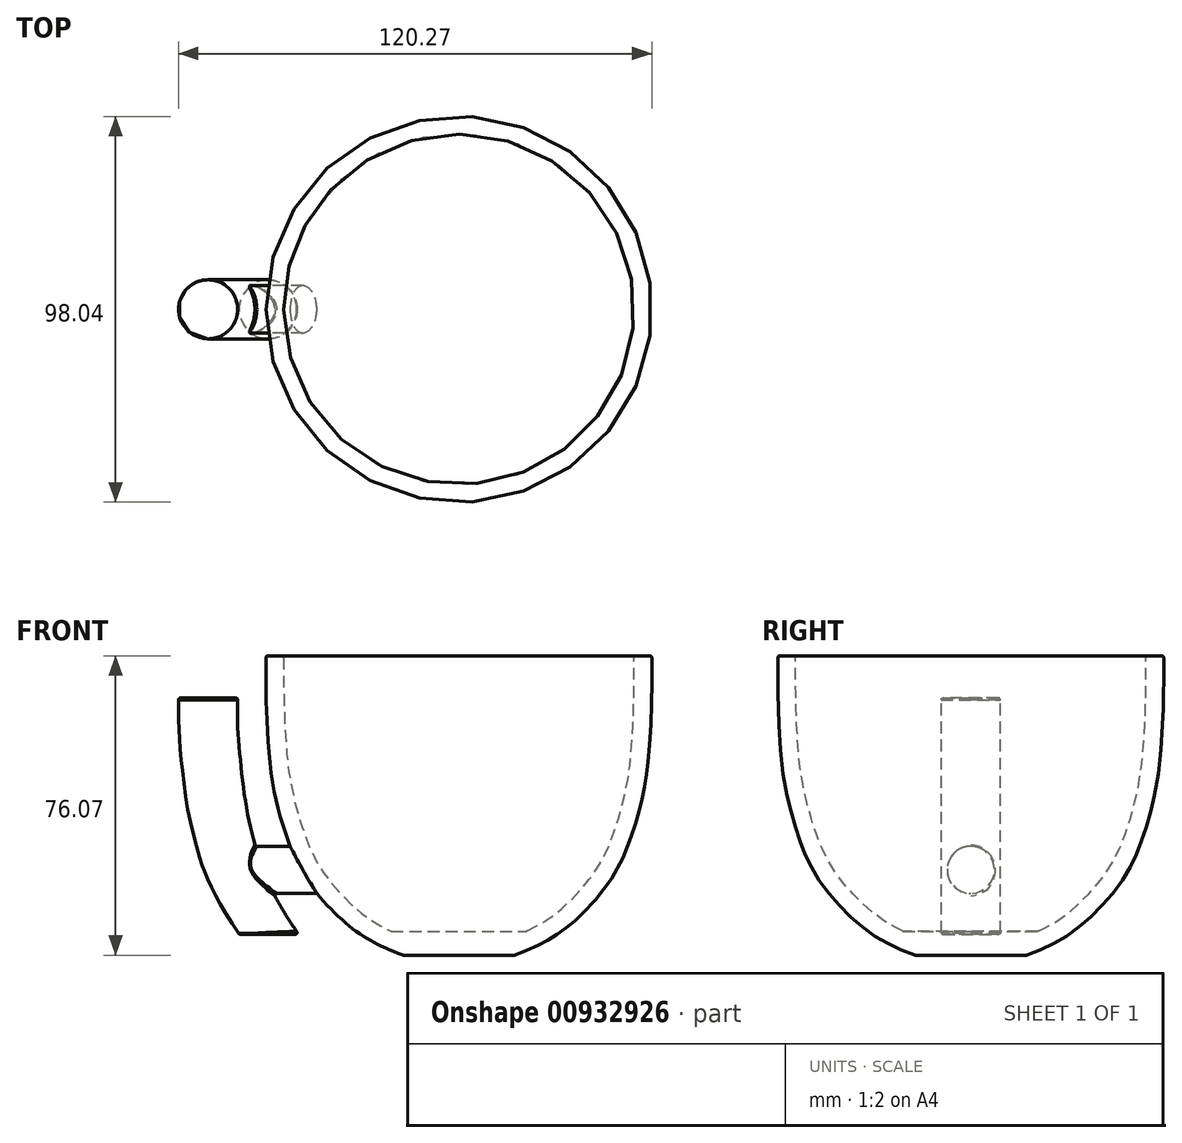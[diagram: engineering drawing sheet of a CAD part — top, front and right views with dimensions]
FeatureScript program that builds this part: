
annotation { "Feature Type Name" : "Feature", "Feature Type Description" : "" }
export const myFeature = defineFeature(function(context is Context, id is Id, definition is map)
    precondition{}
    {
        {
            var Q0;
            Q0=qCreatedBy(makeId("Front.planeOp"),FACE);
            var sketch = newSketch(context, id + "F0", { "sketchPlane" : qUnion([Q0])});
            skLineSegment(sketch, "E0", {"start": v(0, 78.82) * mm, "end": v(-49, 78.82) * mm});
            skLineSegment(sketch, "E1", {"start": v(0, 0) * mm, "end": v(0, 78.82) * mm});
            skFitSpline(sketch, "E2", {"points": [v(-49, 78.82) * mm, v(-49, 71.2) * mm, v(-47.95, 50.94) * mm, v(-44.24, 34.32) * mm, v(-38.54, 21.8) * mm, v(-27.37, 9.77) * mm, v(-17.3, 3.96) * mm, v(0, 0) * mm], "startDerivative": vector(-0.53, -120.05) * mm, "endDerivative": vector(126.32, 0) * mm});
            skSolve(sketch);
        }
        {
            var Q0;
            Q0=qSketchRegion(id+"F0",true);
            var Q1;
            Q1=sQuery(id+"F0.wireOp",EDGE,"E1");
            revolve(context, id + "F1", {"surfaceOperationType" : NewSurfaceOperationType.NEW, "entities" : qUnion([Q0]), "axis" : qUnion([Q1]), "revolveType" : RevolveType.FULL});
        }
        {
            var Q0;
            Q0=makeQuery(id+"F1.opRevolve","SWEPT_FACE",FACE,{"disambiguationData":[OSD([sQuery(id+"F0.wireOp",EDGE,"E0")])]});
            shell(context, id + "F2", {"entities" : qUnion([Q0]), "thickness" : 4.5 * mm});
        }
        {
            var Q0;
            Q0=makeQuery(id+"F1.opRevolve","SWEPT_EDGE",EDGE,{"disambiguationData":[OSD([sQuery(id+"F0.wireOp",EDGE,"E0"),sQuery(id+"F0.wireOp",EDGE,"E2")])]});
            var Q1;
            Q1=makeQuery(id+"F2.opShell","OFFSET_EDGE",EDGE,{"disambiguationData":[OSD([sQuery(id+"F0.wireOp",EDGE,"E0"),sQuery(id+"F0.wireOp",EDGE,"E2")])]});
            fillet(context, id + "F3", {"entities" : qUnion([Q0, Q1]), "radius" : .5 * mm, "tangentPropagation" : true, "defaultsChanged" : true, "vertexSettings" : [], "allowEdgeOverflow" : false});
        }
        {
            var Q0;
            Q0=qCreatedBy(makeId("Front.planeOp"),FACE);
            var sketch = newSketch(context, id + "F4", { "sketchPlane" : qUnion([Q0])});
            skLineSegment(sketch, "E3", {"start": v(-41.77, 30.38) * mm, "end": v(-53.43, 30.38) * mm});
            skLineSegment(sketch, "E4", {"start": v(-49.23, 20.12) * mm, "end": v(-36.53, 20.12) * mm});
            skLineSegment(sketch, "E5", {"start": v(-36.53, 20.12) * mm, "end": v(-41.77, 30.38) * mm});
            skFitSpline(sketch, "E6", {"points": [v(-42.03, 8) * mm, v(-47.44, 16.94) * mm, v(-49.23, 20.12) * mm, v(-51.33, 24.44) * mm, v(-53.43, 30.38) * mm, v(-55.23, 38.72) * mm, v(-56.67, 49.18) * mm, v(-57.32, 61.86) * mm, v(-57.58, 68.13) * mm, v(-57.6, 68.09) * mm], "startDerivative": vector(-47.1, 69.03) * mm, "endDerivative": vector(-6.03, -13.35) * mm});
            skLineSegment(sketch, "E7", {"start": v(-57.58, 68.13) * mm, "end": v(-69.83, 68.13) * mm});
            skFitSpline(sketch, "E8", {"points": [v(-69.83, 68.13) * mm, v(-69.83, 61.07) * mm, v(-69.06, 51.29) * mm, v(-67.63, 40.46) * mm, v(-65.54, 31.18) * mm, v(-63.64, 25) * mm, v(-58.64, 14.66) * mm, v(-54.3, 8) * mm], "startDerivative": vector(-1.12, -53.42) * mm, "endDerivative": vector(31.44, -44.67) * mm});
            skLineSegment(sketch, "E9", {"start": v(-54.3, 8) * mm, "end": v(-42.03, 8) * mm});
            skSolve(sketch);
        }
        {
            var Q0;
            Q0=qCreatedBy(makeId("Right.planeOp"),FACE);
            cPlane(context, id + "F5", {"entities" : qUnion([Q0]), "cplaneType" : CPlaneType.OFFSET, "offset" : 55 * mm, "oppositeDirection" : true, "width" : 150 * mm, "height" : 150 * mm});
        }
        {
            var Q0;
            Q0=qCreatedBy(id+"F5.planeOp",FACE);
            var sketch = newSketch(context, id + "F6", { "sketchPlane" : qUnion([Q0])});
            skPoint(sketch, "E10.middle", {"position": v(0, 24.44) * mm});
            skCircle(sketch, "E11", {"center": v(0, 24.44) * mm, "radius": 6 * mm});
            skSolve(sketch);
        }
        {
            var Q0;
            Q0=qSketchRegion(id+"F6",true);
            extrude(context, id + "F7", {"entities" : qUnion([Q0]), "operationType" : NewBodyOperationType.ADD, "endBound" : BoundingType.UP_TO_NEXT, "depth" : 25 * mm, "offsetDistance" : 25 * mm});
        }
        {
            var Q0;
            Q0=qCreatedBy(makeId("Top.planeOp"),FACE);
            cPlane(context, id + "F8", {"entities" : qUnion([Q0]), "cplaneType" : CPlaneType.OFFSET, "offset" : 8 * mm, "width" : 150 * mm, "height" : 150 * mm});
        }
        {
            var Q0;
            Q0=qCreatedBy(id+"F8.planeOp",FACE);
            var sketch = newSketch(context, id + "F9", { "sketchPlane" : qUnion([Q0])});
            skPoint(sketch, "E12.middle", {"position": v(-48.17, 0) * mm});
            skCircle(sketch, "E13", {"center": v(-48.17, 0) * mm, "radius": 7.5 * mm});
            skSolve(sketch);
        }
        {
            var Q0;
            Q0=qSketchRegion(id+"F9",true);
            var Q1;
            Q1=sQuery(id+"F4.wireOp",EDGE,"E8");
            sweep(context, id + "F10", {"operationType" : NewBodyOperationType.ADD, "profiles" : qUnion([Q0]), "path" : qUnion([Q1]), "keepProfileOrientation" : true});
        }
        {
            var Q0;
            Q0=makeQuery(id+"F10.opSweep","CAP_FACE",FACE,{"disambiguationData":[OSD([sQuery(id+"F4.wireOp",VERTEX,"E8.start"),sQuery(id+"F9.wireOp",EDGE,"E12.bottom"),sQuery(id+"F9.wireOp",EDGE,"E12.top"),sQuery(id+"F9.wireOp",EDGE,"E12.left"),sQuery(id+"F9.wireOp",EDGE,"E12.right")])],"isStart":false});
            var Q1;
            Q1=makeQuery(id+"F10.opSweep","CAP_FACE",FACE,{"disambiguationData":[OSD([sQuery(id+"F4.wireOp",VERTEX,"E8.end"),sQuery(id+"F9.wireOp",EDGE,"E12.bottom"),sQuery(id+"F9.wireOp",EDGE,"E12.top"),sQuery(id+"F9.wireOp",EDGE,"E12.left"),sQuery(id+"F9.wireOp",EDGE,"E12.right")])],"isStart":true});
            fillet(context, id + "F11", {"entities" : qUnion([Q0, Q1]), "radius" : .5 * mm, "tangentPropagation" : true, "defaultsChanged" : true, "vertexSettings" : [], "allowEdgeOverflow" : false});
        }
        {
            var Q0;
            Q0=qCreatedBy(makeId("Front.planeOp"),FACE);
            var sketch = newSketch(context, id + "F12", { "sketchPlane" : qUnion([Q0])});
            skLineSegment(sketch, "E14", {"start": v(0, 1.35) * mm, "end": v(0, 8.85) * mm});
            skLineSegment(sketch, "E15", {"start": v(0, 8.85) * mm, "end": v(-21, 8.85) * mm});
            skLineSegment(sketch, "E16", {"start": v(-21, 8.85) * mm, "end": v(0, 1.35) * mm});
            skSolve(sketch);
        }
        {
            var Q0;
            Q0=qSketchRegion(id+"F12",true);
            var Q1;
            Q1=sQuery(id+"F12.wireOp",EDGE,"E14");
            revolve(context, id + "F13", {"operationType" : NewBodyOperationType.ADD, "surfaceOperationType" : NewSurfaceOperationType.NEW, "entities" : qUnion([Q0]), "axis" : qUnion([Q1]), "revolveType" : RevolveType.FULL});
        }
        {
            var Q0;
            Q0=qCreatedBy(makeId("Front.planeOp"),FACE);
            var sketch = newSketch(context, id + "F14", { "sketchPlane" : qUnion([Q0])});
            skLineSegment(sketch, "E17.bottom", {"start": v(20, 0) * mm, "end": v(-20, 0) * mm});
            skLineSegment(sketch, "E17.top", {"start": v(20, 2.75) * mm, "end": v(-20, 2.75) * mm});
            skLineSegment(sketch, "E17.left", {"start": v(20, 0) * mm, "end": v(20, 2.75) * mm});
            skLineSegment(sketch, "E17.right", {"start": v(-20, 0) * mm, "end": v(-20, 2.75) * mm});
            skSolve(sketch);
        }
        {
            var Q0;
            Q0=qSketchRegion(id+"F14",true);
            extrude(context, id + "F15", {"entities" : qUnion([Q0]), "operationType" : NewBodyOperationType.REMOVE, "oppositeDirection" : true, "depth" : 40 * mm, "offsetDistance" : 25 * mm, "symmetric" : true});
        }
        {
            var Q0;
            Q0=makeQuery(id+"F15.boolean.opBoolean","INTERSECT",EDGE,{"derivedFrom":[makeQuery(id+"F1.opRevolve","SWEPT_FACE",FACE,{"disambiguationData":[OSD([sQuery(id+"F0.wireOp",EDGE,"E2")])]}),makeQuery(id+"F15.opExtrude","SWEPT_FACE",FACE,{"disambiguationData":[OSD([sQuery(id+"F14.wireOp",EDGE,"E17.top")])]})]});
            var Q1;
            Q1=makeQuery(id+"F13.boolean.opBoolean","INTERSECT",EDGE,{"derivedFrom":[makeQuery(id+"F2.opShell","OFFSET_FACE",FACE,{"disambiguationData":[OSD([sQuery(id+"F0.wireOp",EDGE,"E2")])]}),makeQuery(id+"F13.opRevolve","SWEPT_FACE",FACE,{"disambiguationData":[OSD([sQuery(id+"F12.wireOp",EDGE,"E15")])]})]});
            fillet(context, id + "F16", {"entities" : qUnion([Q0, Q1]), "tangentPropagation" : true, "radius" : .5 * mm, "defaultsChanged" : true, "vertexSettings" : [], "allowEdgeOverflow" : false});
        }
        {
            var Q0;
            Q0=makeQuery(id+"F7.opExtrude","CAP_EDGE",EDGE,{"disambiguationData":[OSD([sQuery(id+"F6.wireOp",EDGE,"E11")])],"isStart":false});
            var Q1;
            Q1=makeQuery(id+"F10.boolean.opBoolean","INTERSECT",EDGE,{"derivedFrom":[makeQuery(id+"F7.opExtrude","SWEPT_FACE",FACE,{"disambiguationData":[OSD([sQuery(id+"F6.wireOp",EDGE,"E11")])]}),makeQuery(id+"F10.opSweep","SWEPT_FACE",FACE,{"disambiguationData":[OSD([sQuery(id+"F4.wireOp",EDGE,"E8"),sQuery(id+"F9.wireOp",EDGE,"E13")])]})]});
            fillet(context, id + "F17", {"entities" : qUnion([Q0, Q1]), "tangentPropagation" : true, "radius" : .5 * mm, "defaultsChanged" : true, "vertexSettings" : [], "allowEdgeOverflow" : false});
        }
    });
